# Revit family: IS_Mia_J4694_BIM_DE
name_source: partatom
category: Plumbing Fixtures
revit_build: Autodesk Revit MEP 2016 (Build: 20161004_0715(x64)
units: mm (PartAtom-declared; Revit-internal decimal feet)

## family parameters
Always vertical = No
Cut with Voids When Loaded = No
OmniClass Number = 23.45.05.14.27
OmniClass Title = Bidets
Part Type = Normal
Room Calculation Point = No
Round Connector Dimension = Use Diameter
Shared = No
Work Plane-Based = No

## types (2) — shared parameters
Accessories = www.idealstandard.de\ersatzteile
AssetType = Fixed
BIMobject category = Bidets
BOSUseNativeGeometries = 1
BarCode = 8023246238114
Brand = Ideal Standard
Brand url = http://www.idealstandard.de
CodePerformance = DIN EN 14528 CL 25, DIN EN 35
ConnectionType = Plumbing
CurrencyUnit = €
CurrentRevision = 1
Date of publishing = 20/12/2017
DurationUnit = Year
EAN code = https://8023246238114
Edition number = 1
ExpectedLife = 25
IFC Classification = Sanitary Terminal
IfcExportAs = IfcSanitaryTerminalType
Installation instructions = http://www.idealstandard.de
InstallationInstructions = www.idealstandard.de\produkte
MaintenanceInformation = www.idealstandard.de\produkte
Manufacturer name = Ideal Standard
ManufacturerURL = http://www.idealstandard.de
Material = Vitreous china
Material main = Ceramics
NBS Reference Code = 35-06-11
NBS Reference Description = Bidets
NettWeight = 19 Kg
Nominal height = 310
Nominal width = 360
NominalDepth = 552 mm  [stored 1.81102 ft]
NominalHeight = 310 mm  [stored 1.01706 ft]
NominalLength = 552 mm  [stored 1.81102 ft]
NominalWidth = 359 mm
OmniClass Code = 23-31 23 00
OmniClass Description = Bidets
Product Guid = 1ba42773-c93b-43aa-a538-635cc0191a9e
Product SKU = J4694
Product data url = https://bimobject.com
Product family = Sanitary
Product group = Bidet
Product name = MIA wall mounted bidet 360x550mm, 1 taphole
Product url = http://www.idealstandard.de
ProductInformation = www.idealstandard.de/produkte
QR code = http://bimobject.com
Shape = Sculptured
Size = 359x552x310 mm
Space = Internal
SpareParts = www.idealstandard.de/ersatzteile
Technical description = http://www.idealstandard.de
URL = http://www.idealstandard.de
Uniclass 2.0 Code = PR-35-06-11
Uniclass 2.0 Description = Bidets
Uniclass 2015 Code = Pr_40_20_06_11
Uniclass 2015 Name = Bidets
Uniclass2015Code = Pr_40_20_06_11
Uniclass2015Title = Bidets
Uniclass2015Version = Products v1.1
Version = 1
VolumeUnits = Litres
Weight Net (Kg) = 19
zero-valued in all types: Cost, DrainSize

## per-type parameters (varying)
| type | BIMObjectName | Color | Description | Features | Finish | MainColor | Model | ModelNumber | ModelReference | Name |
| J469401 MIA wall mounted bidet 360x550mm, 1 taphole | ISI_IdealStandard_Bidets_Mia_J469401 | White | IS Wandbidet MIA, 1 Hl., 360x550x310mm, Weiß | IS Wandbidet MIA, 1 Hl., 360x550x310mm, Weiß | White | White | J469401 | J469401 | IS Wandbidet MIA, 1 Hl., 360x550x310mm, Weiß | Bidets_Mia_J469401 |
| J4694MA MIA wall mounted bidet 360x550mm, 1 taphole | ISI_IdealStandard_Bidets_Mia_J4694MA | WHITE IP | IS Wandbidet MIA, 1 Hl., 360x550x310mm, Weiß mit Ideal Plus | IS Wandbidet MIA, 1 Hl., 360x550x310mm, Weiß mit Ideal Plus | WHITE IP | WHITE IP | J4694MA | J4694MA | IS Wandbidet MIA, 1 Hl., 360x550x310mm, Weiß mit Ideal Plus | Bidets_Mia_J4694MA |

note: [stored X ft] marks values corroborated as IEEE doubles in the binary element streams (Revit-internal decimal feet)

## geometry (parser evidence)
native form markers: Blend x4, Sweep x1
no freeform markers — native parametric forms only
